# Revit family: Domotics-DomesticRanges-GEWISS-SYSTEM_CLIMATE-DAILY-WEEKLY_TIMER
name_source: partatom
category: Apparecchi elettrici
revit_build: Autodesk Revit 2016 (Build: 20161004_0715(x64)
units: mm (PartAtom-declared; Revit-internal decimal feet)

## family parameters
Condiviso = Sì
Host = Superficie
Mantenere orientamento annotazione = Sì
Punto di calcolo locali = Sì
Quota connettore circolare = Usa diametro
Taglio con vuoti quando caricato = Sì
Tipo di parte = Normale

## types (2) — shared parameters
Carico apparente = 0 VA
Catalogue = DOMOTICS
Catalogue Range = SYSTEM - DOMESTIC RANGE
Description. = Programmer
Electrocod = 0141
IDF = 3da45d71-4361-468b-99e1-3980742295c6
IDT = 13de42dd-8a5e-4a41-bce1-4adb09ffc7f1
Immagine tipo = GW21825.jpg
N. poli = 1
No. SYSTEM modules = 2
Produttore = GEWISS S.p.A.
Prospetto di default = 1219 mm
SEO = Programmer
Supply voltage = 230 V ac - 50/60 Hz
TIPO = System Programmatore_GENERICO : GW21825 Programmatore elettronico giornaliero/settimanale 1 canale 230V nero
Technical sheet = https://www.gewiss.com
URL = https://www.gewiss.com
Version file RFA = 19.4
Volt = 230 V

## per-type parameters (varying)
| type | Colour | Descrizione | EAN code | Modello | Shape |
| GW21825 - Dly/wkly electronic timer 1channel b | Black | DLY/WKLY ELECTRONIC TIMER 1CHANNEL B | 8011564439818 | GW21825 | Aligned vertical |
| GW20825 - Dly/wkly electronic timer 1channel w | White | DLY/WKLY ELECTRONIC TIMER 1CHANNEL W | 8011564439801 | GW20825 | Parallel horizontal |

## geometry (parser evidence)
native form markers: Sweep x1
no freeform markers — native parametric forms only
